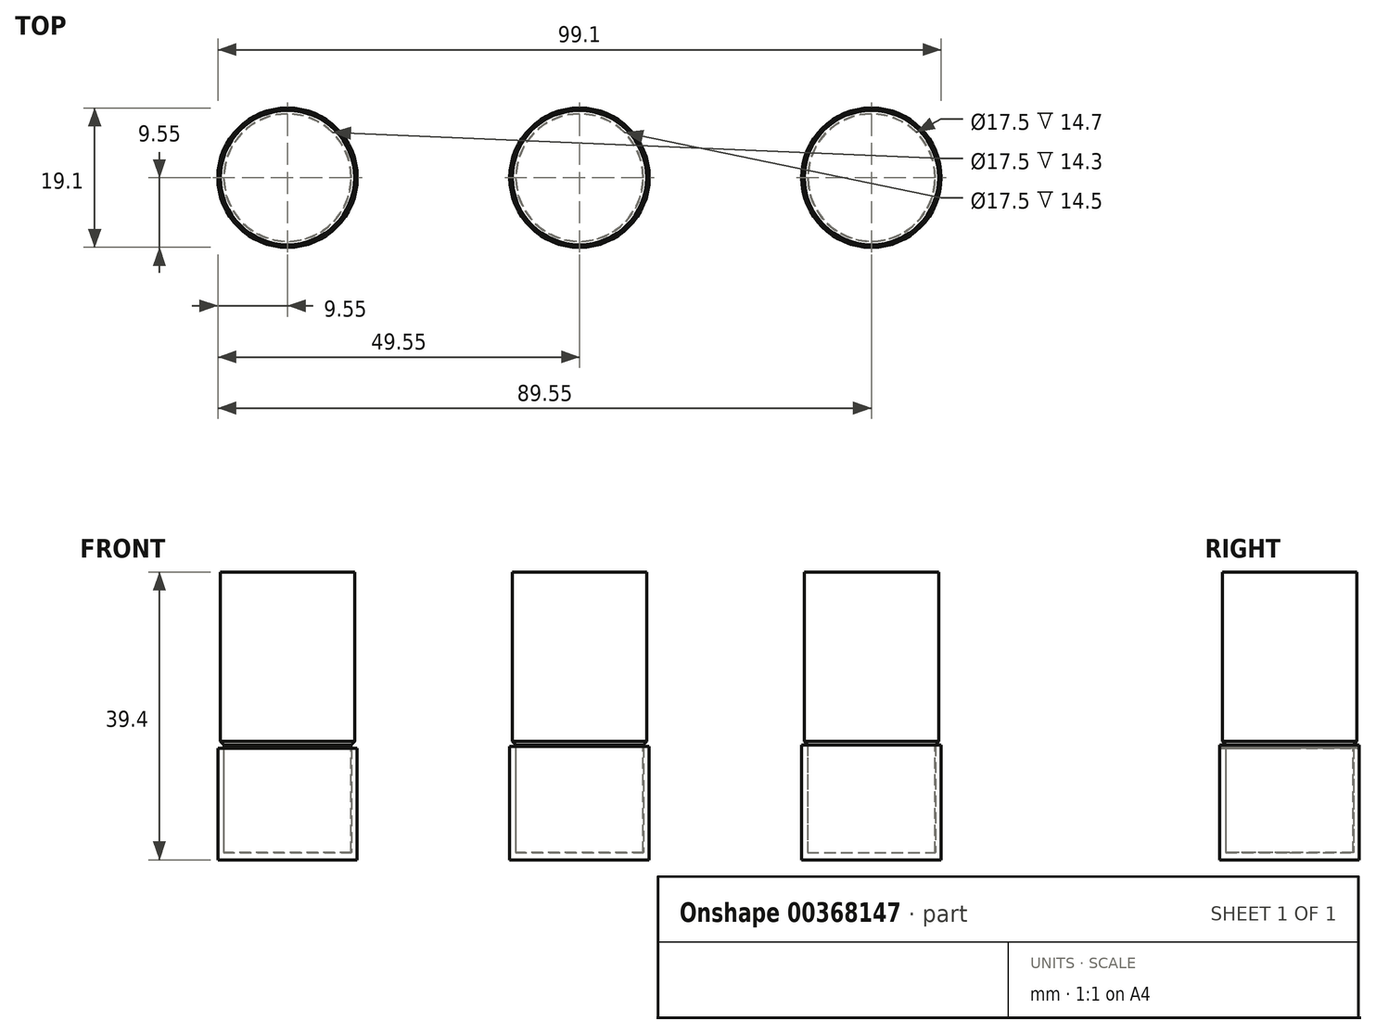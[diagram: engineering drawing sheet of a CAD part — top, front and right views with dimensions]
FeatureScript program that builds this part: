
annotation { "Feature Type Name" : "Feature", "Feature Type Description" : "" }
export const myFeature = defineFeature(function(context is Context, id is Id, definition is map)
    precondition{}
    {
        {
            var Q0;
            Q0=qCreatedBy(makeId("Front.planeOp"),FACE);
            var sketch = newSketch(context, id + "F0", { "sketchPlane" : qUnion([Q0])});
            skLineSegment(sketch, "E0.bottom", {"start": v(0, 0) * mm, "end": v(9.55, 0) * mm});
            skLineSegment(sketch, "E0.right", {"start": v(9.55, 0) * mm, "end": v(9.55, 15.5) * mm});
            skLineSegment(sketch, "E1", {"start": v(9.55, 15.5) * mm, "end": v(8.75, 15.5) * mm});
            skLineSegment(sketch, "E2", {"start": v(8.75, 15.5) * mm, "end": v(8.75, 1) * mm});
            skLineSegment(sketch, "E3", {"start": v(8.75, 1) * mm, "end": v(0, 1) * mm});
            skLineSegment(sketch, "E4", {"start": v(0, 1) * mm, "end": v(0, 0) * mm});
            skLineSegment(sketch, "E5", {"start": v(0, 0) * mm, "end": v(0, 11.58) * mm, "construction": true});
            skSolve(sketch);
        }
        {
            var Q0;
            Q0 = qSketchRegion(id + "F0", true);
            var Q1;
            Q1=sQuery(id+"F0.wireOp",EDGE,"E5");
            revolve(context, id + "F1", {"entities" : qUnion([Q0]), "axis" : qUnion([Q1]), "revolveType" : RevolveType.FULL});
        }
        {
            var Q0;
            Q0=qCreatedBy(makeId("Front.planeOp"),FACE);
            var sketch = newSketch(context, id + "F2", { "sketchPlane" : qUnion([Q0])});
            skLineSegment(sketch, "E6", {"start": v(-40, 0) * mm, "end": v(-30.45, 0) * mm});
            skLineSegment(sketch, "E7", {"start": v(-30.45, 0) * mm, "end": v(-30.45, 15.3) * mm});
            skLineSegment(sketch, "E8", {"start": v(-30.45, 15.3) * mm, "end": v(-31.25, 15.3) * mm});
            skLineSegment(sketch, "E9", {"start": v(-31.25, 15.3) * mm, "end": v(-31.25, 1) * mm});
            skLineSegment(sketch, "E10", {"start": v(-31.25, 1) * mm, "end": v(-40, 1) * mm});
            skLineSegment(sketch, "E11", {"start": v(-40, 1) * mm, "end": v(-40, 0) * mm});
            skLineSegment(sketch, "E12", {"start": v(-40, 0) * mm, "end": v(-40, 13.5) * mm, "construction": true});
            skSolve(sketch);
        }
        {
            var Q0;
            Q0 = qSketchRegion(id + "F2", true);
            var Q1;
            Q1=sQuery(id+"F2.wireOp",EDGE,"E12");
            revolve(context, id + "F3", {"entities" : qUnion([Q0]), "axis" : qUnion([Q1]), "revolveType" : RevolveType.FULL});
        }
        {
            var Q0;
            Q0=qCreatedBy(makeId("Front.planeOp"),FACE);
            var sketch = newSketch(context, id + "F4", { "sketchPlane" : qUnion([Q0])});
            skLineSegment(sketch, "E13", {"start": v(40, 0) * mm, "end": v(40, 13.83) * mm, "construction": true});
            skLineSegment(sketch, "E14", {"start": v(40, 0) * mm, "end": v(40, 1) * mm});
            skLineSegment(sketch, "E15", {"start": v(40, 1) * mm, "end": v(48.75, 1) * mm});
            skLineSegment(sketch, "E16", {"start": v(48.75, 1) * mm, "end": v(48.75, 15.7) * mm});
            skLineSegment(sketch, "E17", {"start": v(48.75, 15.7) * mm, "end": v(49.55, 15.7) * mm});
            skLineSegment(sketch, "E18", {"start": v(49.55, 15.7) * mm, "end": v(49.55, 0) * mm});
            skLineSegment(sketch, "E19", {"start": v(49.55, 0) * mm, "end": v(40, 0) * mm});
            skSolve(sketch);
        }
        {
            var Q0;
            Q0 = qSketchRegion(id + "F4", true);
            var Q1;
            Q1=sQuery(id+"F4.wireOp",EDGE,"E13");
            revolve(context, id + "F5", {"entities" : qUnion([Q0]), "axis" : qUnion([Q1]), "revolveType" : RevolveType.FULL});
        }
        {
            var Q0;
            Q0=qCreatedBy(makeId("Front.planeOp"),FACE);
            var sketch = newSketch(context, id + "F6", { "sketchPlane" : qUnion([Q0])});
            skLineSegment(sketch, "E20", {"start": v(-40, 0) * mm, "end": v(-40, 35.74) * mm, "construction": true});
            skLineSegment(sketch, "E21", {"start": v(-40, 1) * mm, "end": v(-31.3, 1) * mm});
            skLineSegment(sketch, "E22", {"start": v(-31.3, 1) * mm, "end": v(-31.3, 15.7) * mm});
            skLineSegment(sketch, "E23", {"start": v(-31.3, 15.7) * mm, "end": v(-30.8, 16.2) * mm});
            skLineSegment(sketch, "E24", {"start": v(-30.8, 16.2) * mm, "end": v(-30.8, 39.4) * mm});
            skLineSegment(sketch, "E25", {"start": v(-30.8, 39.4) * mm, "end": v(-40, 39.4) * mm});
            skLineSegment(sketch, "E26", {"start": v(-40, 39.4) * mm, "end": v(-40, 1) * mm});
            skLineSegment(sketch, "E27", {"start": v(-31.3, 15.7) * mm, "end": v(-31.3, 17.36) * mm, "construction": true});
            skSolve(sketch);
        }
        {
            var Q0;
            Q0=makeQuery(id+"F6.imprint","IMPRINT",FACE,{"disambiguationData":[TD([[makeQuery(id+"F6.imprint","IMPRINT",EDGE,{"derivedFrom":sQuery(id+"F6.wireOp",EDGE,"E21")}),1.0]])]});
            var Q1;
            Q1=sQuery(id+"F6.wireOp",EDGE,"E26");
            revolve(context, id + "F7", {"operationType" : NewBodyOperationType.ADD, "entities" : qUnion([Q0]), "axis" : qUnion([Q1]), "revolveType" : RevolveType.FULL});
        }
        {
            var Q0;
            Q0=qCreatedBy(makeId("Front.planeOp"),FACE);
            var sketch = newSketch(context, id + "F8", { "sketchPlane" : qUnion([Q0])});
            skLineSegment(sketch, "E28", {"start": v(0, 26.75) * mm, "end": v(0, 0) * mm, "construction": true});
            skLineSegment(sketch, "E29", {"start": v(0, 1) * mm, "end": v(8.7, 1) * mm});
            skLineSegment(sketch, "E30", {"start": v(8.7, 1) * mm, "end": v(8.7, 15.7) * mm});
            skLineSegment(sketch, "E31", {"start": v(8.7, 15.7) * mm, "end": v(9.2, 16.2) * mm});
            skLineSegment(sketch, "E32", {"start": v(9.2, 16.2) * mm, "end": v(9.2, 39.4) * mm});
            skLineSegment(sketch, "E33", {"start": v(9.2, 39.4) * mm, "end": v(0, 39.4) * mm});
            skLineSegment(sketch, "E34", {"start": v(0, 39.4) * mm, "end": v(0, 1) * mm});
            skLineSegment(sketch, "E35", {"start": v(8.7, 15.7) * mm, "end": v(8.7, 16.59) * mm, "construction": true});
            skSolve(sketch);
        }
        {
            var Q0;
            Q0 = qSketchRegion(id + "F8", true);
            var Q1;
            Q1=sQuery(id+"F8.wireOp",EDGE,"E34");
            revolve(context, id + "F9", {"operationType" : NewBodyOperationType.ADD, "entities" : qUnion([Q0]), "axis" : qUnion([Q1]), "revolveType" : RevolveType.FULL});
        }
        {
            var Q0;
            Q0=qCreatedBy(makeId("Front.planeOp"),FACE);
            var sketch = newSketch(context, id + "F10", { "sketchPlane" : qUnion([Q0])});
            skLineSegment(sketch, "E36", {"start": v(40, 0) * mm, "end": v(40, 43.23) * mm, "construction": true});
            skLineSegment(sketch, "E37", {"start": v(40, 1) * mm, "end": v(48.7, 1) * mm});
            skLineSegment(sketch, "E38", {"start": v(48.7, 1) * mm, "end": v(48.7, 15.7) * mm});
            skLineSegment(sketch, "E39", {"start": v(48.7, 15.7) * mm, "end": v(49.2, 16.2) * mm});
            skLineSegment(sketch, "E40", {"start": v(49.2, 16.2) * mm, "end": v(49.2, 39.4) * mm});
            skLineSegment(sketch, "E41", {"start": v(49.2, 39.4) * mm, "end": v(40, 39.4) * mm});
            skLineSegment(sketch, "E42", {"start": v(40, 39.4) * mm, "end": v(40, 1) * mm});
            skLineSegment(sketch, "E43", {"start": v(48.7, 15.7) * mm, "end": v(48.7, 20.96) * mm, "construction": true});
            skSolve(sketch);
        }
        {
            var Q0;
            Q0 = qSketchRegion(id + "F10", true);
            var Q1;
            Q1=sQuery(id+"F10.wireOp",EDGE,"E42");
            revolve(context, id + "F11", {"operationType" : NewBodyOperationType.ADD, "entities" : qUnion([Q0]), "axis" : qUnion([Q1]), "revolveType" : RevolveType.FULL});
        }
    });
